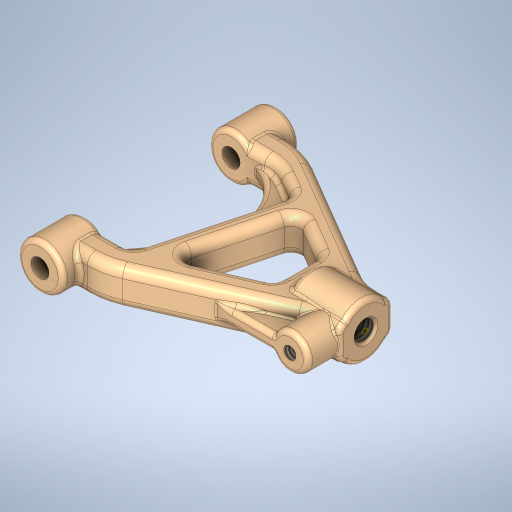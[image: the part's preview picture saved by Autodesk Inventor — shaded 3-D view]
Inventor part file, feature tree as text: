
AUTODESK INVENTOR PART (.ipt)
format: ipt  version: 2024 (Build 280153000, 153)  size: 1,507,328 bytes
history: native  units: in
note: dims shown in document units (in); Inventor stores cm internally (conversion verified against a paired STEP export)
features: fillet x19, sketch x9, extrude x6, projected_geometry x4, rib x3, plane x2, hole x2, chamfer x1, direct_edit x1, other x1
ambient origin geometry x8: Origin, YZ Plane, XZ Plane, XY Plane, X Axis, Y Axis, Z Axis, Center Point
bodies: Solid1 (feature_tree)
feature tree (48):
  extrude  "Extrusion1"  Depth=0.315in TaperAngle=0.0deg
  plane  "Work Plane1"
  extrude  "Extrusion2"  Depth=0.315in TaperAngle=0.0deg
  extrude  "Extrusion3"  Depth=0.375in
  fillet  "Fillet1"  Radius=0.5in
  fillet  "Fillet2"  Radius=1.5in
  fillet  "Fillet3"  Radius=0.188in
  fillet  "Fillet4"  Radius=0.315in
  fillet  "Fillet5"  Radius=0.2in
  fillet  "Fillet6"  Radius=0.2in
  fillet  "Fillet7"  [1 undecoded]
  rib  "Rib1"
  fillet  "Fillet8"  Radius=0.15in
  rib  "Rib2"
  fillet  "Fillet9"  Radius=0.25in
  sketch  "Sketch13"  dims[d6=0.742in d7=0.375in d8=0.5in d9=1.5in d10=0.188in d11=0.315in d12=0.2in d13=0.2in d14=105.0deg d15=0.15in d16=0.25in d17=0.0in]
  extrude  "Extrusion4"  Depth=0.5in
  fillet  "Fillet10"  Radius=0.0625in
  fillet  "Fillet11"  Radius=0.315in
  fillet  "Fillet12"  Radius=0.0625in
  fillet  "Fillet13"  Radius=0.0625in
  fillet  "Fillet14"  Radius=0.032in
  extrude  "Extrusion5"  Depth=0.357in
  plane  "Work Plane2"
  extrude  "Extrusion6"  Depth=0.1in
  fillet  "Fillet15"  Radius=0.032in
  rib  "Rib3"
  fillet  "Fillet16"  Radius=0.125in
  fillet  "Fillet17"  Radius=0.188in
  fillet  "Fillet18"  Radius=0.375in
  hole  "Hole1"  [1 undecoded]
  fillet  "Fillet19"  Radius=0.032in
  hole  "Hole2"  [1 undecoded]
  chamfer  "Chamfer1"  Distance=0.032in
  direct_edit  "Direct Edit1"
  sketch  "Sketch4"  dims[d0=0.315in d1=0.315in d2=0.0in]
  projected_geometry  "Projected Loop1"
  projected_geometry  "Projected Loop2"
  projected_geometry  "Projected Loop3"
  sketch  "Sketch12"  dims[d3=1.0in d4=0.315in d5=0.0in]
  sketch  "Sketch14"  dims[d18=0.315in d19=0.5in d20=0.0625in d21=0.315in d22=0.0625in d23=0.0625in d24=0.032in]
  sketch  "Sketch15"  dims[d25=0.1in]
  sketch  "Sketch16"  dims[d26=0.1in d27=0.0in d28=0.0in d29=0.1in d30=0.1in d31=0.357in]
  sketch  "Sketch17"  dims[d32=0.032in d37=0.1in]
  sketch  "Sketch18"  dims[d38=0.1in d39=0.0in d40=0.0in d41=0.1in d42=0.1in d43=0.032in d45=0.125in d46=0.188in d47=0.375in]
  sketch  "Sketch19"  dims[d48=0.3875in d49=0.0in d50=0.032in d51=0.032in d52=0.032in d53=0.032in d54=0.032in d55=0.125in d56=100.0in d57=0.0in d58=0.2in d59=0.25in d60=0.135in d61=100.0in d62=0.0in d63=0.015in d64=0.1in d65=0.1in d66=0.0in d67=0.0in d68=0.1in d69=0.1in d70=0.014in d71=0.032in d72=0.032in d73=0.0849in d74=0.25in d75=0.375in d76=0.25in d77=0.5635in d78=0.25in d79=0.8108in d80=0.014in d81=0.134in d82=0.328in d83=0.375in d84=0.25in d85=0.5635in d86=0.375in d87=0.8108in d88=0.015in d89=0.125in d90=45.0deg d91=3.937in d92=0.3937in d93=0.3937in]
  projected_geometry  "Project Cut Edges1"
  other  "Scale1"
note: 3 required parameter values undecoded (feature->parameter linkage not recoverable at this tier; creation-order binding heuristic only, values carry confidence <= 0.55)
